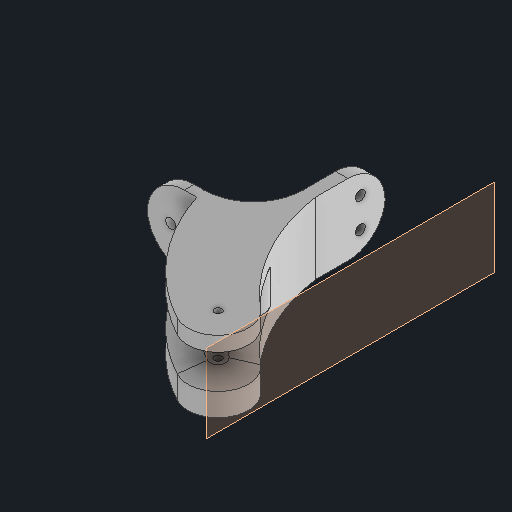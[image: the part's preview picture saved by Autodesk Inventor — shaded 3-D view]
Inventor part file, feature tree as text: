
AUTODESK INVENTOR PART (.ipt)
format: ipt  version: 2024 (Build 280153000, 153)  size: 243,200 bytes
history: native  units: mm
features: other x10, reference x10, extrude x6, sketch x6, fillet x3, chamfer x2
ambient origin geometry x8: Origin, YZ Plane, XZ Plane, XY Plane, X Axis, Y Axis, Z Axis, Center Point
bodies: Body1 (feature_tree)
feature tree (37):
  other  "Твердое тело1"
  extrude  "Выдавливание1"  Depth=28.75mm TaperAngle=0.0deg
  other  "РабПлоскость2"
  extrude  "Выдавливание4"  Depth=5.0mm
  fillet  "Сопряжение1"  Radius=20.0mm
  extrude  "Выдавливание5"  Depth=80.0mm
  extrude  "Выдавливание6"  Depth=25.0mm
  extrude  "Выдавливание7"  Depth=80.0mm
  fillet  "Сопряжение2"  Radius=50.0mm
  extrude  "Выдавливание8"  Depth=85.0mm TaperAngle=0.0deg
  fillet  "Сопряжение3"  Radius=15.0mm
  chamfer  "Фаска1"  Distance=3.0mm
  chamfer  "Фаска2"  Distance=5.5mm
  sketch  "Эскиз1"
  reference  "Ссылка1"
  reference  "Ссылка2"
  reference  "Ссылка3"
  reference  "Ссылка4"
  reference  "Ссылка5"
  sketch  "Эскиз4"
  reference  "Ссылка8"
  reference  "Ссылка9"
  sketch  "Эскиз6"
  sketch  "Эскиз7"
  reference  "Ссылка10"
  sketch  "Эскиз8"
  sketch  "Эскиз9"
  reference  "Ссылка11"
  reference  "Ссылка12"
  parser-record x1  (decoder bookkeeping rows leaked as tree rows — omitted from the tree; the rows remain in map.json)
  other  "main_assembly.iam"
  other  "manipulator:1"
  other  "platform:2"
  other  "base_assambly:1"
  other  "fb_axis:2"
  other  "arm_assembly_l:2"
  other  "motor_holder_l:1"
note: 1 file-system path scrubbed to <path> (originals preserved in map.json)
